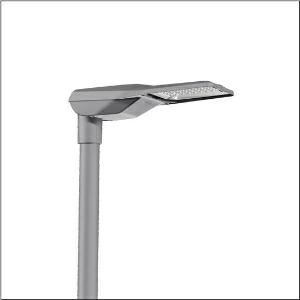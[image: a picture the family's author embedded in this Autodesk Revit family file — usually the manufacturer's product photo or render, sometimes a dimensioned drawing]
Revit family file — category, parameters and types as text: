
# Revit family: streetlight_sl_21_iq_mini___pl52_5xe2h41g08gb_5dc3
name_source: partatom
category: Lighting Fixtures
units: mm (PartAtom-declared; Revit-internal decimal feet)

## family parameters
Cut with Voids When Loaded = No
Host = Face
Light Source = No
Part Type = Normal
Room Calculation Point = No
Round Connector Dimension = Use Diameter
Shared = No

## types (1)
- --- (1 x LED, 5810 lm, 37.1 W, 4000K)
    Apparent Load = 37 VA
    CIE Flux Codes = 27 59 98 100 100
    Color Rendering = 70
    Color Temperature = 4000K
    Default Elevation = 1800 mm
    Description = Streetlight SL 21 iQ mini, mast luminaire, primary light control with lens, of PMMA, primary optical cover: cover, of toughened safety glass, transparent, light distribution: PL52, light emission: direct distribution, primary light characteristic: asymmetric, installation type: post-top, side-entry, LED, High Power LED, rated luminous flux: 5.810lm, luminous efficacy: 157lm/W, light colour: 740, colour temperature: 4000K, control: Street-Remote, Auto-Match, Temp-Guard, Lumen-Switch, Night-Set, Smart-Wire, Light-Fading, Desk-Remote (wireless, voltage-free reading and setting of iQ features in the workshop via application-optimized NFC function/RFID function), optimised constant luminous flux control (CLO 2.0), presetting dimming linear, mains connection: 220..240V, AC, 50/60Hz, start of lifetime: 37W, end of service life: 39W, reduction: 18W, luminaire housing, of diecast aluminium, powder-coated, Siteco® metallic grey (DB 702S), corrosivity category C5 mid according to DIN EN ISO 12944, please order mast flange separately, inclination adjustable: 0°, 5°, 10°, 15°, sealing non-destructively replaceable, multi-level sealing system, length: 628mm, width: 235mm, height: 110mm, mast flange for spigot size: 42mm (side-entry): 5XC10008XM4, 60/48mm (side-entry/post-top): 5XC10108XM2, 76/60mm (side-entry/post-top): 5XC10108XM1, protection rating (complete): IP66, insulation class (complete): insulation class II (safety insulation), certification: CE, ENEC, ENEC+, VDE, impact resistance: IK09, permissible operating ambient temperature for outdoor applications: -40..+50°C, standard-compliant lighting for roads and squares, packaging unit: 1 piece

Light Distribution: PL52
    Height = 110 mm
    Lamp = 1 x LED
    Lamp Light Flux = 5810 lm
    Lamp Power = 37.1 W
    Lamp count = 1
    Length = 625 mm
    Luminous efficacy = 157 lm/W
    Manufacturer = Siteco
    ModVariant = No
    Model = 5XE2H41G08GB
    Number of Poles = 1
    OnlyDefault = Yes
    Power Factor = 1
    Product Name = Streetlight SL 21 iQ mini | PL52
    Product group = mast luminaire | pylon top
    ProductGroupID = 6100
    Protection Class = Protection class II
    Protection Degree = IP 66
    RLX_Detail_Level = 1
    RLX_Emergency_Light_Flux = 0 lm
    RLX_Emergency_Type = 0
    RLX_Emergency_Type_DB = No
    RlxData = <blob elided: 102101 chars, md5=185d3a7a>
    Socket = socket
    Standby Power = 0 W
    System Light Flux = 5810 lm
    System Power = 37 W
    Type Comments = factory setting: luminous flux: 100 % | dim-lin: 254 | 385 mA
    Type Image = l_1003519.jpg
    URL = http://relux.com
    VarID = @adj_124235
    Voltage = 0 V
    Weight = 0.00 kg
    Width = 234 mm

## geometry (parser evidence)
native form markers: Blend x4, Sweep x10
no freeform markers — native parametric forms only
